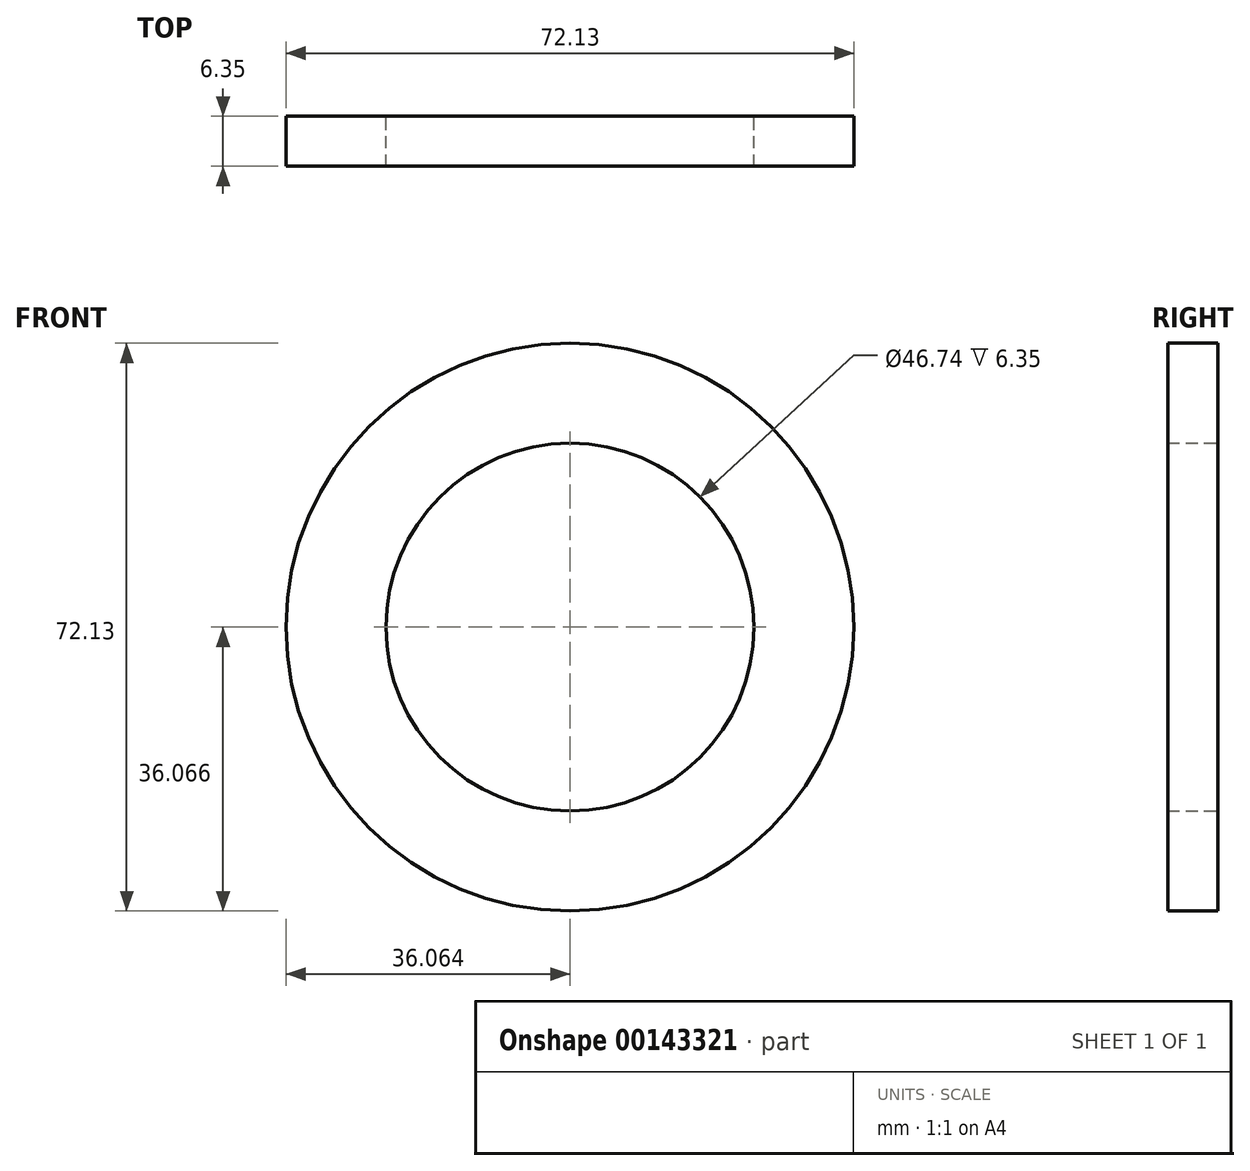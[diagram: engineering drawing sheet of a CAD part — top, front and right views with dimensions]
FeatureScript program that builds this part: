
annotation { "Feature Type Name" : "Feature", "Feature Type Description" : "" }
export const myFeature = defineFeature(function(context is Context, id is Id, definition is map)
    precondition{}
    {
        {
            var Q0;
            Q0=qCreatedBy(makeId("Front.planeOp"),FACE);
            var sketch = newSketch(context, id + "F0", { "sketchPlane" : qUnion([Q0])});
            skCircle(sketch, "E0", {"center": v(-16.49, -6.65) * mm, "radius": 36.07 * mm});
            skCircle(sketch, "E1", {"center": v(-16.49, -6.65) * mm, "radius": 23.37 * mm});
            skSolve(sketch);
        }
        {
            var Q0;
            Q0=makeQuery(id+"F0.imprint","IMPRINT",FACE,{"disambiguationData":[TD([[makeQuery(id+"F0.imprint","IMPRINT",EDGE,{"derivedFrom":sQuery(id+"F0.wireOp",EDGE,"E0")}),1.0]])]});
            extrude(context, id + "F1", {"entities" : qUnion([Q0]), "depth" : 6.35 * mm});
        }
    });
